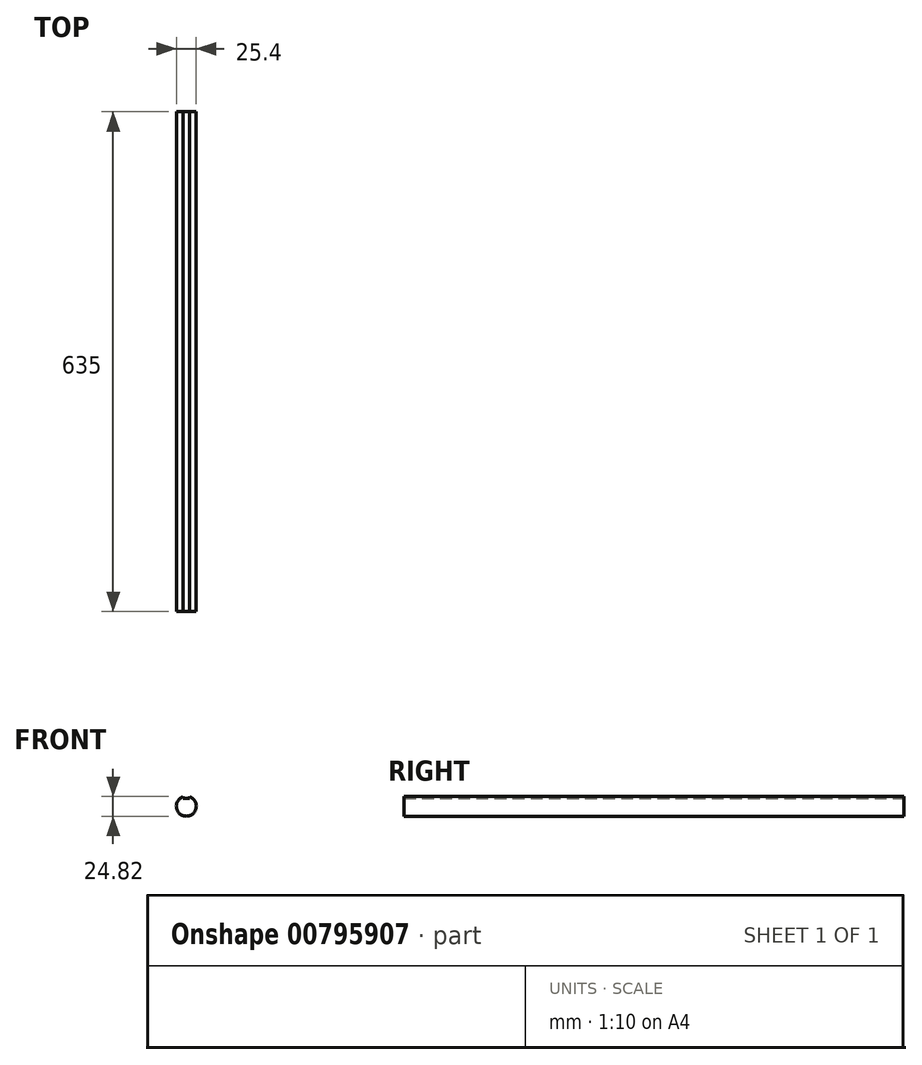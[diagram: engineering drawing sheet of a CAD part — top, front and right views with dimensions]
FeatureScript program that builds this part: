
annotation { "Feature Type Name" : "Feature", "Feature Type Description" : "" }
export const myFeature = defineFeature(function(context is Context, id is Id, definition is map)
    precondition{}
    {
        {
            var Q0;
            Q0=qCreatedBy(makeId("Front.planeOp"),FACE);
            var sketch = newSketch(context, id + "F0", { "sketchPlane" : qUnion([Q0])});
            skArc(sketch, "E0", {"start": v(-3.8, 12.12) * mm, "mid": v(0, -12.7) * mm, "end": v(3.81, 12.12) * mm});
            skLineSegment(sketch, "E1.top", {"start": v(3.81, 10.16) * mm, "end": v(-3.81, 10.16) * mm});
            skLineSegment(sketch, "E1.left", {"start": v(3.81, 12.12) * mm, "end": v(3.81, 10.16) * mm});
            skLineSegment(sketch, "E1.right", {"start": v(-3.81, 12.12) * mm, "end": v(-3.81, 10.16) * mm});
            skPoint(sketch, "E1.middle", {"position": v(0, 12.7) * mm});
            skPoint(sketch, "E1.bottom.start.orphan", {"position": v(3.8, 15.24) * mm});
            skPoint(sketch, "E2.orphan", {"position": v(-3.81, 15.24) * mm});
            skSolve(sketch);
        }
        {
            var Q0;
            Q0=makeQuery(id+"F0.imprint","IMPRINT",FACE,{"disambiguationData":[TD([[makeQuery(id+"F0.imprint","IMPRINT",EDGE,{"derivedFrom":sQuery(id+"F0.wireOp",EDGE,"E0")}),1.0]])]});
            extrude(context, id + "F1", {"entities" : qUnion([Q0]), "depth" : 635 * mm, "offsetDistance" : 25.4 * mm});
        }
    });
